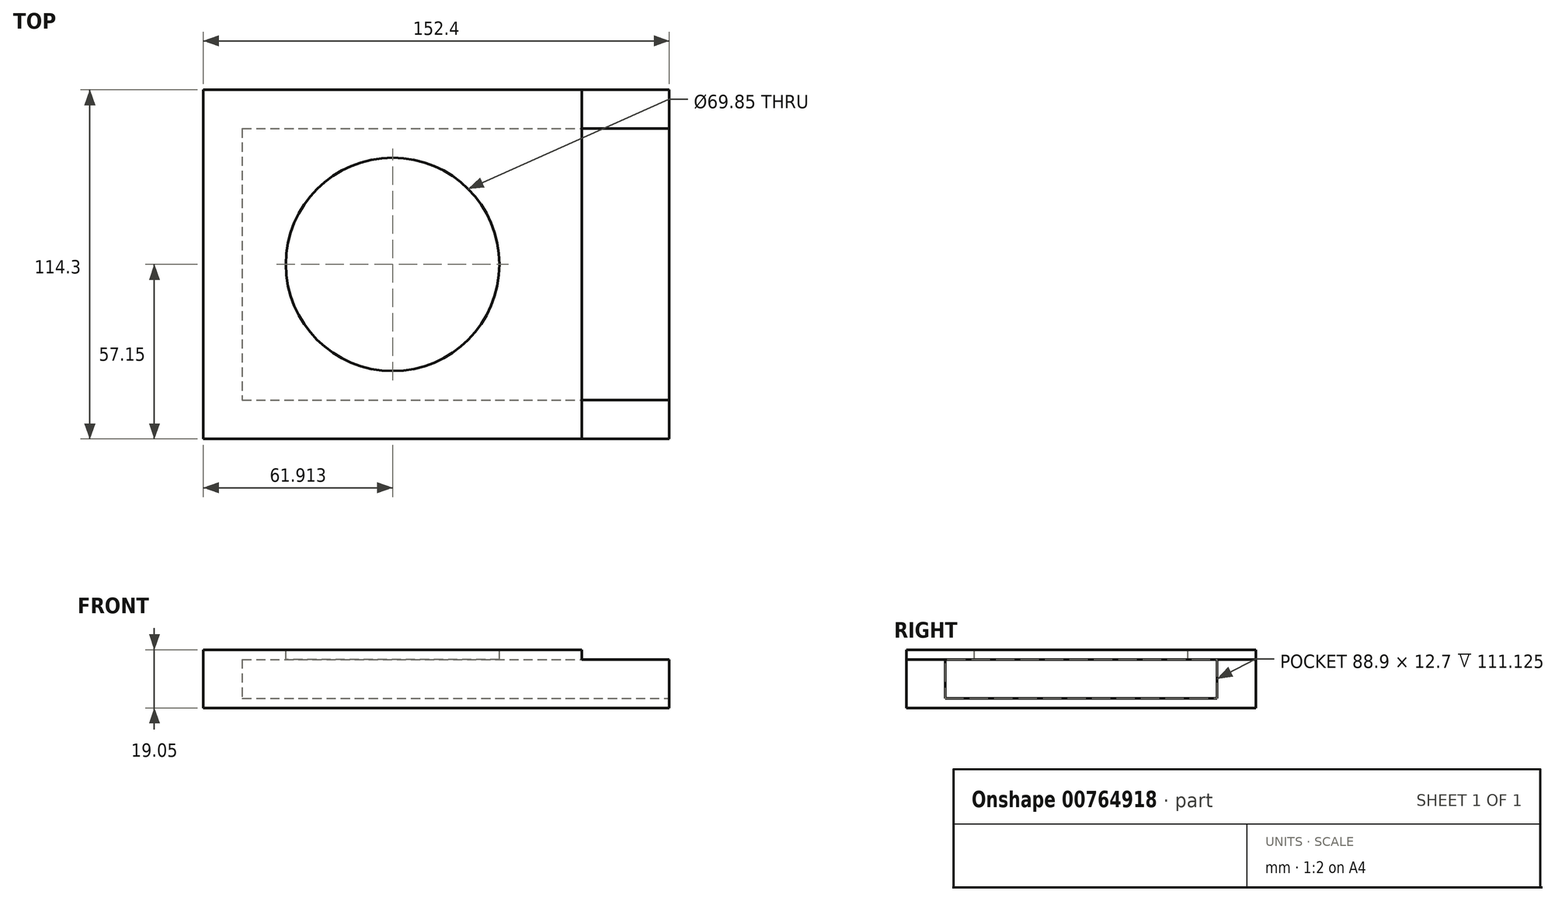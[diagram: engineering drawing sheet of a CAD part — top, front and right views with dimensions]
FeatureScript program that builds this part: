
annotation { "Feature Type Name" : "Feature", "Feature Type Description" : "" }
export const myFeature = defineFeature(function(context is Context, id is Id, definition is map)
    precondition{}
    {
        {
            var Q0;
            Q0=qCreatedBy(makeId("Top.planeOp"),FACE);
            var sketch = newSketch(context, id + "F0", { "sketchPlane" : qUnion([Q0])});
            skLineSegment(sketch, "E0.bottom", {"start": v(76.2, -57.15) * mm, "end": v(-76.2, -57.15) * mm});
            skLineSegment(sketch, "E0.top", {"start": v(76.2, 57.15) * mm, "end": v(-76.2, 57.15) * mm});
            skLineSegment(sketch, "E0.left", {"start": v(76.2, -57.15) * mm, "end": v(76.2, 57.15) * mm});
            skLineSegment(sketch, "E0.right", {"start": v(-76.2, -57.15) * mm, "end": v(-76.2, 57.15) * mm});
            skPoint(sketch, "E0.middle", {"position": v(0, 0) * mm});
            skSolve(sketch);
        }
        {
            var Q0;
            Q0 = qSketchRegion(id + "F0", true);
            extrude(context, id + "F1", {"entities" : qUnion([Q0]), "depth" : 3.17 * mm, "offsetDistance" : 25.4 * mm});
        }
        {
            var Q0;
            Q0=makeQuery(id+"F1.opExtrude","CAP_FACE",FACE,{"disambiguationData":[OSD([sQuery(id+"F0.wireOp",EDGE,"E0.bottom"),sQuery(id+"F0.wireOp",EDGE,"E0.top"),sQuery(id+"F0.wireOp",EDGE,"E0.left"),sQuery(id+"F0.wireOp",EDGE,"E0.right")])],"isStart":false});
            var sketch = newSketch(context, id + "F2", { "sketchPlane" : qUnion([Q0])});
            skLineSegment(sketch, "E1.bottom", {"start": v(-76.2, -57.15) * mm, "end": v(76.2, -57.15) * mm});
            skLineSegment(sketch, "E1.top", {"start": v(-76.2, -44.45) * mm, "end": v(76.2, -44.45) * mm});
            skLineSegment(sketch, "E1.left", {"start": v(-76.2, -57.15) * mm, "end": v(-76.2, -44.45) * mm});
            skLineSegment(sketch, "E1.right", {"start": v(76.2, -57.15) * mm, "end": v(76.2, -44.45) * mm});
            skLineSegment(sketch, "E2.bottom", {"start": v(-76.2, 57.15) * mm, "end": v(76.2, 57.15) * mm});
            skLineSegment(sketch, "E2.top", {"start": v(-76.2, 44.45) * mm, "end": v(76.2, 44.45) * mm});
            skLineSegment(sketch, "E2.left", {"start": v(-76.2, 57.15) * mm, "end": v(-76.2, 44.45) * mm});
            skLineSegment(sketch, "E2.right", {"start": v(76.2, 57.15) * mm, "end": v(76.2, 44.45) * mm});
            skSolve(sketch);
        }
        {
            var Q0;
            Q0 = qSketchRegion(id + "F2", true);
            extrude(context, id + "F3", {"entities" : qUnion([Q0]), "operationType" : NewBodyOperationType.ADD, "depth" : 12.7 * mm, "offsetDistance" : 25.4 * mm});
        }
        {
            var Q0;
            Q0=makeQuery(id+"F1.opExtrude","CAP_FACE",FACE,{"disambiguationData":[OSD([sQuery(id+"F0.wireOp",EDGE,"E0.bottom"),sQuery(id+"F0.wireOp",EDGE,"E0.top"),sQuery(id+"F0.wireOp",EDGE,"E0.left"),sQuery(id+"F0.wireOp",EDGE,"E0.right")])],"isStart":false});
            var sketch = newSketch(context, id + "F4", { "sketchPlane" : qUnion([Q0])});
            skLineSegment(sketch, "E3.bottom", {"start": v(-76.2, 44.45) * mm, "end": v(-63.5, 44.45) * mm});
            skLineSegment(sketch, "E3.top", {"start": v(-76.2, -44.45) * mm, "end": v(-63.5, -44.45) * mm});
            skLineSegment(sketch, "E3.left", {"start": v(-76.2, 44.45) * mm, "end": v(-76.2, -44.45) * mm});
            skLineSegment(sketch, "E3.right", {"start": v(-63.5, 44.45) * mm, "end": v(-63.5, -44.45) * mm});
            skSolve(sketch);
        }
        {
            var Q0;
            Q0 = qSketchRegion(id + "F4", true);
            extrude(context, id + "F5", {"entities" : qUnion([Q0]), "operationType" : NewBodyOperationType.ADD, "depth" : 12.7 * mm, "offsetDistance" : 25.4 * mm});
        }
        {
            var Q0;
            Q0=makeQuery(id+"F5.boolean.opBoolean","MERGE",FACE,{"derivedFrom":[makeQuery(id+"F3.opExtrude","CAP_FACE",FACE,{"disambiguationData":[OSD([sQuery(id+"F2.wireOp",EDGE,"E1.bottom"),sQuery(id+"F2.wireOp",EDGE,"E1.top"),sQuery(id+"F2.wireOp",EDGE,"E1.left"),sQuery(id+"F2.wireOp",EDGE,"E1.right")])],"isStart":false}),makeQuery(id+"F3.opExtrude","CAP_FACE",FACE,{"disambiguationData":[OSD([sQuery(id+"F2.wireOp",EDGE,"E2.bottom"),sQuery(id+"F2.wireOp",EDGE,"E2.top"),sQuery(id+"F2.wireOp",EDGE,"E2.left"),sQuery(id+"F2.wireOp",EDGE,"E2.right")])],"isStart":false}),makeQuery(id+"F5.opExtrude","CAP_FACE",FACE,{"disambiguationData":[OSD([sQuery(id+"F4.wireOp",EDGE,"E3.bottom"),sQuery(id+"F4.wireOp",EDGE,"E3.top"),sQuery(id+"F4.wireOp",EDGE,"E3.left"),sQuery(id+"F4.wireOp",EDGE,"E3.right")])],"isStart":false})]});
            var sketch = newSketch(context, id + "F6", { "sketchPlane" : qUnion([Q0])});
            skLineSegment(sketch, "E4.bottom", {"start": v(-76.2, -57.15) * mm, "end": v(47.63, -57.15) * mm});
            skLineSegment(sketch, "E4.top", {"start": v(-76.2, 57.15) * mm, "end": v(47.62, 57.15) * mm});
            skLineSegment(sketch, "E4.left", {"start": v(-76.2, -57.15) * mm, "end": v(-76.2, 57.15) * mm});
            skLineSegment(sketch, "E4.right", {"start": v(47.63, -57.15) * mm, "end": v(47.62, 57.15) * mm});
            skSolve(sketch);
        }
        {
            var Q0;
            Q0 = qSketchRegion(id + "F6", true);
            extrude(context, id + "F7", {"entities" : qUnion([Q0]), "operationType" : NewBodyOperationType.ADD, "depth" : 3.17 * mm, "offsetDistance" : 25.4 * mm});
        }
        {
            var Q0;
            Q0=makeQuery(id+"F7.opExtrude","CAP_FACE",FACE,{"disambiguationData":[OSD([sQuery(id+"F6.wireOp",EDGE,"E4.bottom"),sQuery(id+"F6.wireOp",EDGE,"E4.top"),sQuery(id+"F6.wireOp",EDGE,"E4.left"),sQuery(id+"F6.wireOp",EDGE,"E4.right")])],"isStart":false});
            var sketch = newSketch(context, id + "F8", { "sketchPlane" : qUnion([Q0])});
            skLineSegment(sketch, "E5", {"start": v(-14.29, 57.15) * mm, "end": v(-14.29, -57.15) * mm, "construction": true});
            skCircle(sketch, "E6", {"center": v(-14.29, 0) * mm, "radius": 34.93 * mm});
            skSolve(sketch);
        }
        {
            var Q0;
            Q0=makeQuery(id+"F8.imprint","IMPRINT",FACE,{"disambiguationData":[TD([[makeQuery(id+"F8.imprint","IMPRINT",EDGE,{"derivedFrom":sQuery(id+"F8.wireOp",EDGE,"E6")}),1.0]])]});
            extrude(context, id + "F9", {"entities" : qUnion([Q0]), "operationType" : NewBodyOperationType.REMOVE, "oppositeDirection" : true, "depth" : 3.17 * mm, "offsetDistance" : 25.4 * mm});
        }
    });
